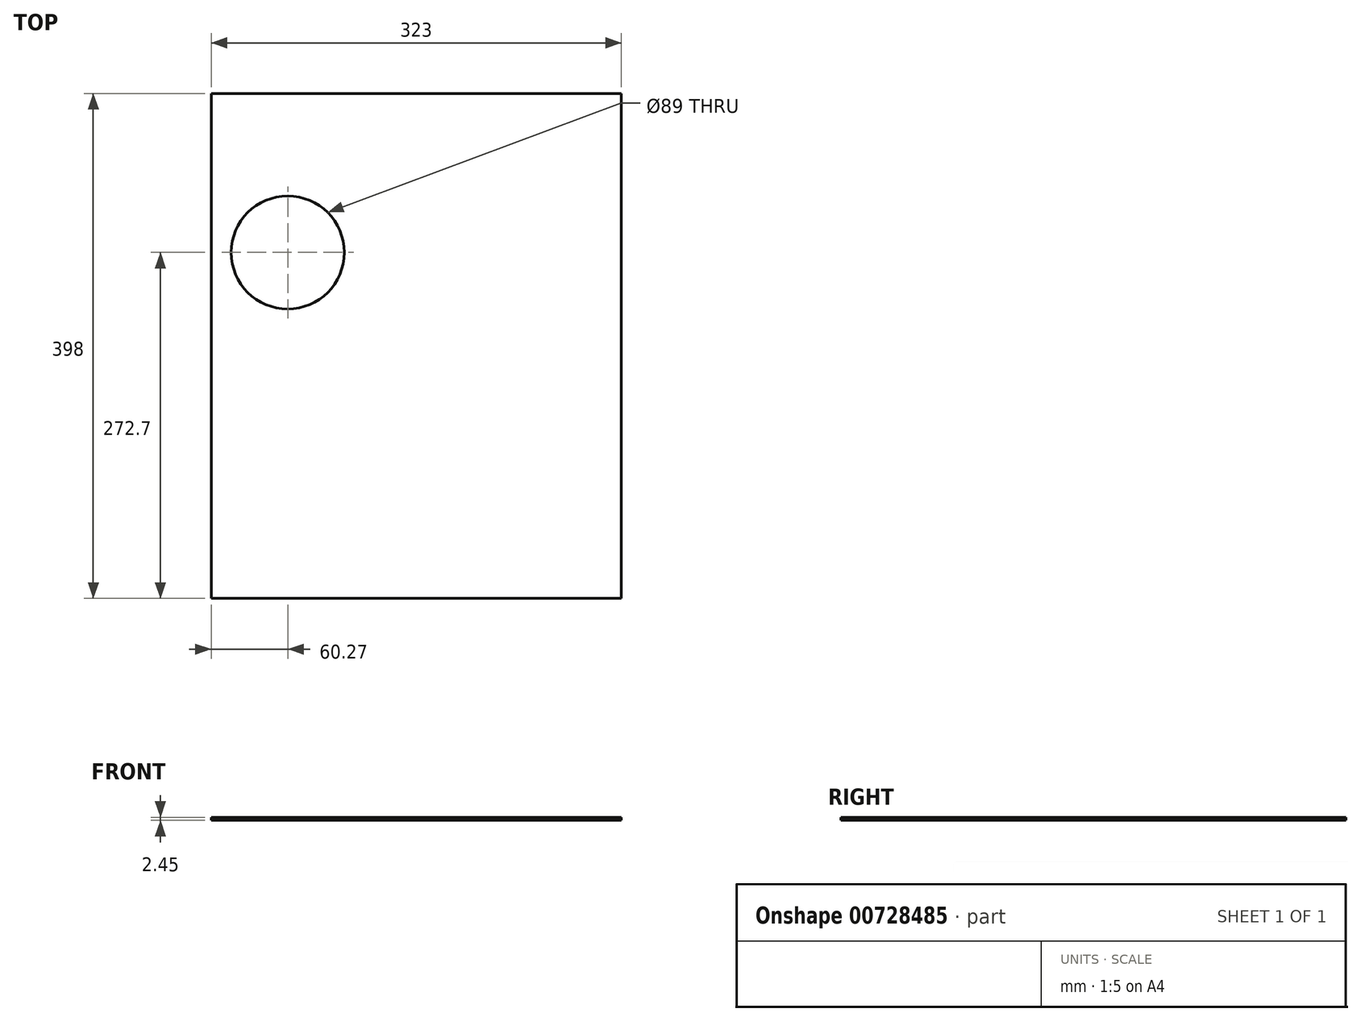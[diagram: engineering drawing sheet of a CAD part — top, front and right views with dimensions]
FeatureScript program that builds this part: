
annotation { "Feature Type Name" : "Feature", "Feature Type Description" : "" }
export const myFeature = defineFeature(function(context is Context, id is Id, definition is map)
    precondition{}
    {
        {
            var Q0;
            Q0=qCreatedBy(makeId("Top.planeOp"),FACE);
            var sketch = newSketch(context, id + "F0", { "sketchPlane" : qUnion([Q0])});
            skLineSegment(sketch, "E0.bottom", {"start": v(0, 0) * mm, "end": v(323, 0) * mm});
            skLineSegment(sketch, "E0.top", {"start": v(0, -398) * mm, "end": v(323, -398) * mm});
            skLineSegment(sketch, "E0.left", {"start": v(0, 0) * mm, "end": v(0, -398) * mm});
            skLineSegment(sketch, "E0.right", {"start": v(323, 0) * mm, "end": v(323, -398) * mm});
            skPoint(sketch, "E1", {"position": v(60.27, -125.3) * mm});
            skCircle(sketch, "E2", {"center": v(60.27, -125.3) * mm, "radius": 44.5 * mm});
            skSolve(sketch);
        }
        {
            var Q0;
            Q0=makeQuery(id+"F0.imprint","IMPRINT",FACE,{"disambiguationData":[TD([[makeQuery(id+"F0.imprint","IMPRINT",EDGE,{"derivedFrom":sQuery(id+"F0.wireOp",EDGE,"E0.bottom")}),-1.0]])]});
            extrude(context, id + "F1", {"entities" : qUnion([Q0]), "depth" : 2.45 * mm, "offsetDistance" : 25 * mm});
        }
    });
